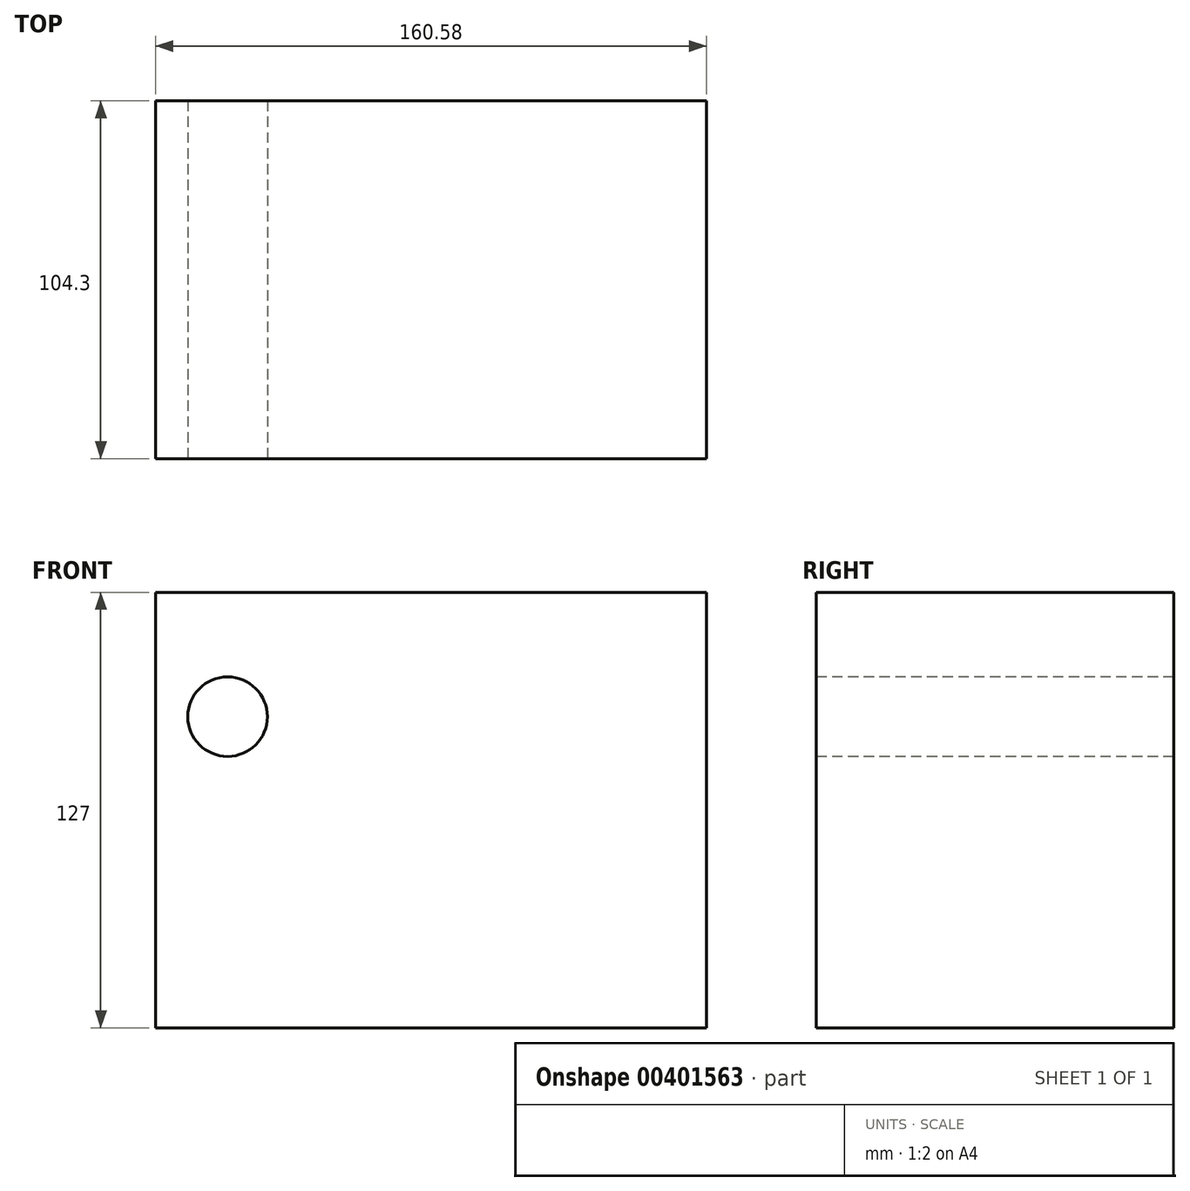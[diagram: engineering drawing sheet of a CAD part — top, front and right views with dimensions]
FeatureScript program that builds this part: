
annotation { "Feature Type Name" : "Feature", "Feature Type Description" : "" }
export const myFeature = defineFeature(function(context is Context, id is Id, definition is map)
    precondition{}
    {
        {
            var Q0;
            Q0=qCreatedBy(makeId("Top.planeOp"),FACE);
            var sketch = newSketch(context, id + "F0", { "sketchPlane" : qUnion([Q0])});
            skLineSegment(sketch, "E0.bottom", {"start": v(80.3, -52.15) * mm, "end": v(-80.3, -52.15) * mm});
            skLineSegment(sketch, "E0.top", {"start": v(80.3, 52.15) * mm, "end": v(-80.3, 52.15) * mm});
            skLineSegment(sketch, "E0.left", {"start": v(80.3, -52.15) * mm, "end": v(80.3, 52.15) * mm});
            skLineSegment(sketch, "E0.right", {"start": v(-80.3, -52.15) * mm, "end": v(-80.3, 52.15) * mm});
            skPoint(sketch, "E0.middle", {"position": v(0, 0) * mm});
            skSolve(sketch);
        }
        {
            var Q0;
            Q0 = qSketchRegion(id + "F0", true);
            extrude(context, id + "F1", {"entities" : qUnion([Q0]), "depth" : 127 * mm});
        }
        {
            var Q0;
            Q0=makeQuery(id+"F1.opExtrude","SWEPT_FACE",FACE,{"disambiguationData":[OSD([sQuery(id+"F0.wireOp",EDGE,"E0.bottom")])]});
            var sketch = newSketch(context, id + "F2", { "sketchPlane" : qUnion([Q0])});
            skCircle(sketch, "E1", {"center": v(-59.35, 90.73) * mm, "radius": 11.6 * mm});
            skSolve(sketch);
        }
        {
            var Q0;
            Q0 = qSketchRegion(id + "F2", true);
            extrude(context, id + "F3", {"entities" : qUnion([Q0]), "operationType" : NewBodyOperationType.REMOVE, "oppositeDirection" : true, "depth" : 163.32 * mm});
        }
    });
